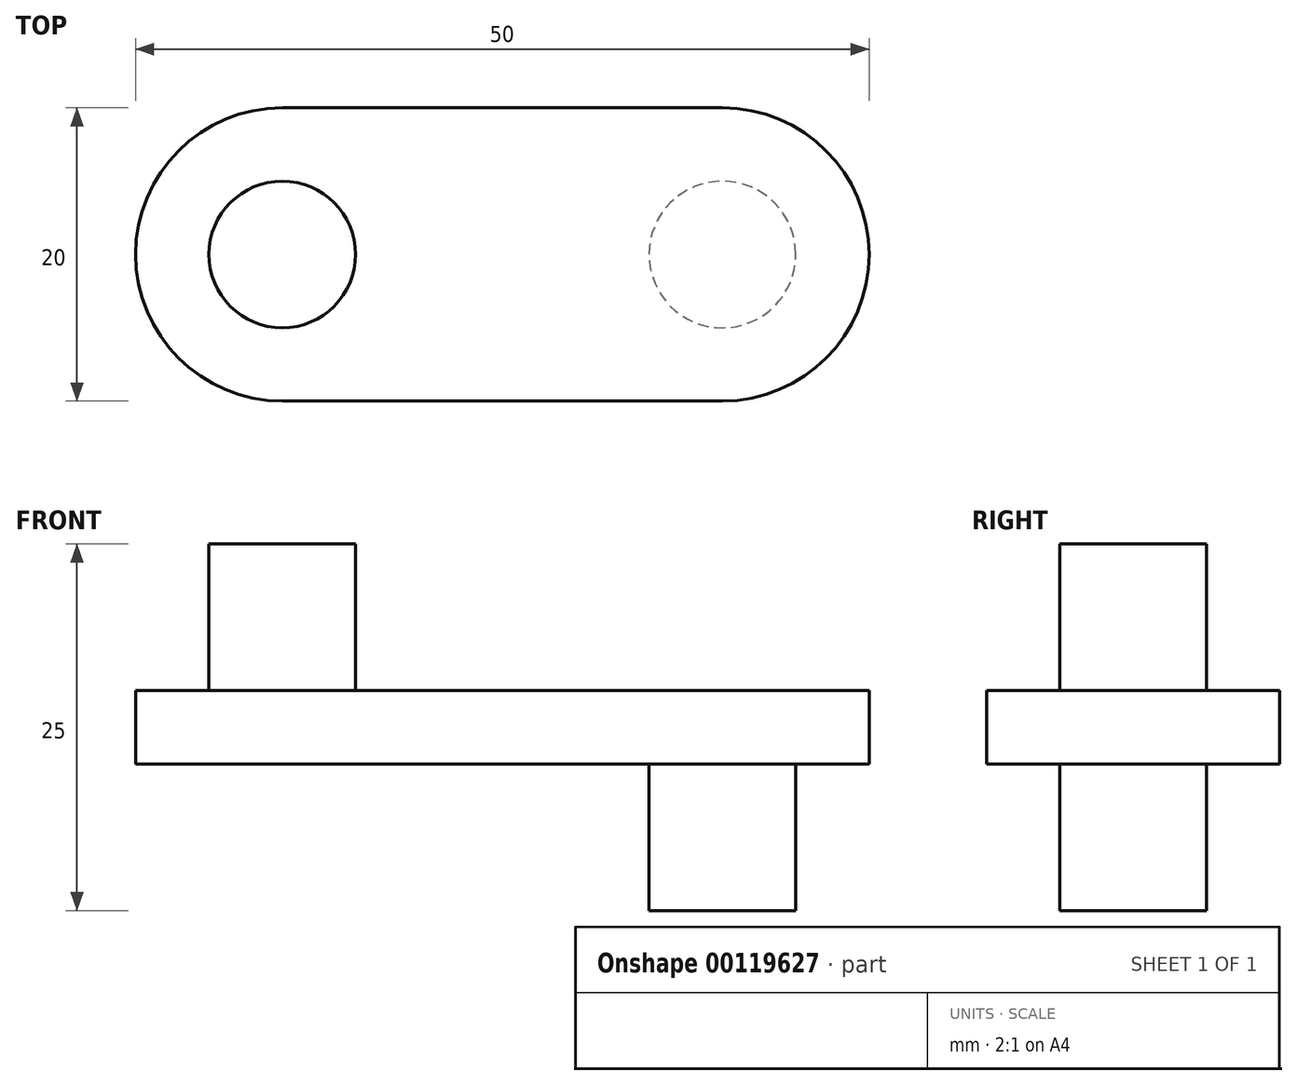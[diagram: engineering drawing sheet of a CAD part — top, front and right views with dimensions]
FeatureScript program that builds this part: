
annotation { "Feature Type Name" : "Feature", "Feature Type Description" : "" }
export const myFeature = defineFeature(function(context is Context, id is Id, definition is map)
    precondition{}
    {
        {
            var Q0;
            Q0=qCreatedBy(makeId("Top.planeOp"),FACE);
            var sketch = newSketch(context, id + "F0", { "sketchPlane" : qUnion([Q0])});
            skLineSegment(sketch, "E0", {"start": v(0, 0) * mm, "end": v(30, 0) * mm});
            skLineSegment(sketch, "E1", {"start": v(30, 20) * mm, "end": v(0, 20) * mm});
            skArc(sketch, "E2", {"start": v(30, 0) * mm, "mid": v(40, 10) * mm, "end": v(30, 20) * mm});
            skArc(sketch, "E3", {"start": v(0, 20) * mm, "mid": v(-10, 10) * mm, "end": v(0, 0) * mm});
            skSolve(sketch);
        }
        {
            var Q0;
            Q0 = qSketchRegion(id + "F0", true);
            extrude(context, id + "F1", {"entities" : qUnion([Q0]), "depth" : 5 * mm});
        }
        {
            var Q0;
            Q0=makeQuery(id+"F1.opExtrude","CAP_FACE",FACE,{"disambiguationData":[OSD([sQuery(id+"F0.wireOp",EDGE,"E0"),sQuery(id+"F0.wireOp",EDGE,"E1"),sQuery(id+"F0.wireOp",EDGE,"E2"),sQuery(id+"F0.wireOp",EDGE,"E3")])],"isStart":false});
            var sketch = newSketch(context, id + "F2", { "sketchPlane" : qUnion([Q0])});
            skCircle(sketch, "E4", {"center": v(0, 10) * mm, "radius": 5 * mm});
            skSolve(sketch);
        }
        {
            var Q0;
            Q0=makeQuery(id+"F2.imprint","IMPRINT",FACE,{"disambiguationData":[TD([[makeQuery(id+"F2.imprint","IMPRINT",EDGE,{"derivedFrom":sQuery(id+"F2.wireOp",EDGE,"E4")}),1.0]])]});
            extrude(context, id + "F3", {"entities" : qUnion([Q0]), "operationType" : NewBodyOperationType.ADD, "depth" : 10 * mm});
        }
        {
            var Q0;
            Q0=makeQuery(id+"F1.opExtrude","CAP_FACE",FACE,{"disambiguationData":[OSD([sQuery(id+"F0.wireOp",EDGE,"E0"),sQuery(id+"F0.wireOp",EDGE,"E1"),sQuery(id+"F0.wireOp",EDGE,"E2"),sQuery(id+"F0.wireOp",EDGE,"E3")])],"isStart":true});
            var sketch = newSketch(context, id + "F4", { "sketchPlane" : qUnion([Q0])});
            skCircle(sketch, "E5", {"center": v(30, -10) * mm, "radius": 5 * mm});
            skSolve(sketch);
        }
        {
            var Q0;
            Q0=makeQuery(id+"F4.imprint","IMPRINT",FACE,{"disambiguationData":[TD([[makeQuery(id+"F4.imprint","IMPRINT",EDGE,{"derivedFrom":sQuery(id+"F4.wireOp",EDGE,"E5")}),1.0]])]});
            extrude(context, id + "F5", {"entities" : qUnion([Q0]), "operationType" : NewBodyOperationType.ADD, "depth" : 10 * mm});
        }
    });
